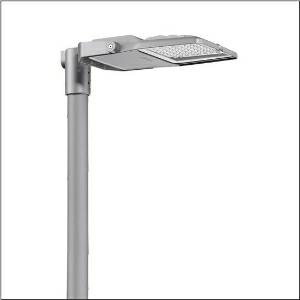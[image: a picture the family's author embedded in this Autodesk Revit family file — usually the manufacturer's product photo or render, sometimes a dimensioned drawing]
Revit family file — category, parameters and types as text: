
# Revit family: floodlight_fl_21_iq_mini___pl43_5xa7772b4a3a_1e53
name_source: partatom
category: Lighting Fixtures
units: mm (PartAtom-declared; Revit-internal decimal feet)

## family parameters
Cut with Voids When Loaded = No
Host = Face
Light Source = No
Part Type = Normal
Room Calculation Point = No
Round Connector Dimension = Use Diameter
Shared = No

## types (1)
- --- (1 x LED, 6660 lm, 45.5 W, 4000K)
    Apparent Load = 46 VA
    CIE Flux Codes = 27 78 99 100 100
    Color Rendering = 70
    Color Temperature = 4000K
    Default Elevation = 1800 mm
    Description = Floodlight FL 21 iQ mini, floodlight, primary light control with lens, of PMMA, primary optical cover: protective disc, of toughened safety glass, transparent, light distribution: PL43, light emission: direct distribution, installation type: surface-mounted, LED, High Power LED, rated luminous flux: 6.660lm, luminous efficacy: 146lm/W, light colour: 740, colour temperature: 4000K, control gear: iQ Street-Remote/DALI, control: Auto-Match, Temp-Guard, Night-Set, Smart-Wire, Desk-Remote (wireless, voltage-free reading and setting of iQ features in the workshop via application-optimized NFC function/RFID function), optimised constant luminous flux control (CLO 2.0), Light-Fading, Lumen-Switch, with terminal, 6-pole, mains connection: 220..240V, AC, 50/60Hz, start of lifetime: 46W, end of service life: 48W, reduction: 22W, luminaire housing, of diecast aluminium, powder-coated, Siteco® metallic grey (DB 702S), corrosivity category C5 mid according to DIN EN ISO 12944, suitable for swimming pools, chlorine-resistant, sealing non-destructively replaceable, please order mast flange separately, mast bracket, of steel, galvanised, powder-coated, protection rating (complete): IP66, insulation class (complete): insulation class II (safety insulation), certification: CE, ENEC, VDE, protection symbol: D, impact resistance: IK08, permissible operating ambient temperature: -40..+40°C, permissible operating ambient temperature for outdoor applications: -40..+50°C, standard: DIN EN 12944, LABS conformity tested according to VDMA 24364:2018-05, packaging unit: 1 piece

Light Distribution: PL43
    Height = 70 mm
    Lamp = 1 x LED
    Lamp Light Flux = 6660 lm
    Lamp Power = 45.5 W
    Lamp count = 1
    Length = 485 mm
    Luminous efficacy = 146 lm/W
    Manufacturer = Siteco
    ModVariant = No
    Model = 5XA7772B4A3A
    Number of Poles = 1
    OnlyDefault = Yes
    Power Factor = 1
    Product Name = Floodlight FL 21 iQ mini | PL43
    Product group = floodlight | pylon annexe
    ProductGroupID = 6200
    Protection Class = Protection class II
    Protection Degree = IP 66
    RLX_Detail_Level = 1
    RLX_Emergency_Light_Flux = 0 lm
    RLX_Emergency_Type = 0
    RLX_Emergency_Type_DB = No
    RlxData = <blob elided: 101201 chars, md5=c6c16a50>
    Socket = socket
    Standby Power = 0 W
    System Light Flux = 6660 lm
    System Power = 46 W
    Type Comments = factory setting: luminous flux: 100 % | dim-lin: 254 | 463 mA
    Type Image = l_1007125.jpg
    URL = http://relux.com
    VarID = @adj_162682
    Voltage = 0 V
    Weight = 0.00 kg
    Width = 337 mm

## geometry (parser evidence)
native form markers: Blend x4, Sweep x11
no freeform markers — native parametric forms only
